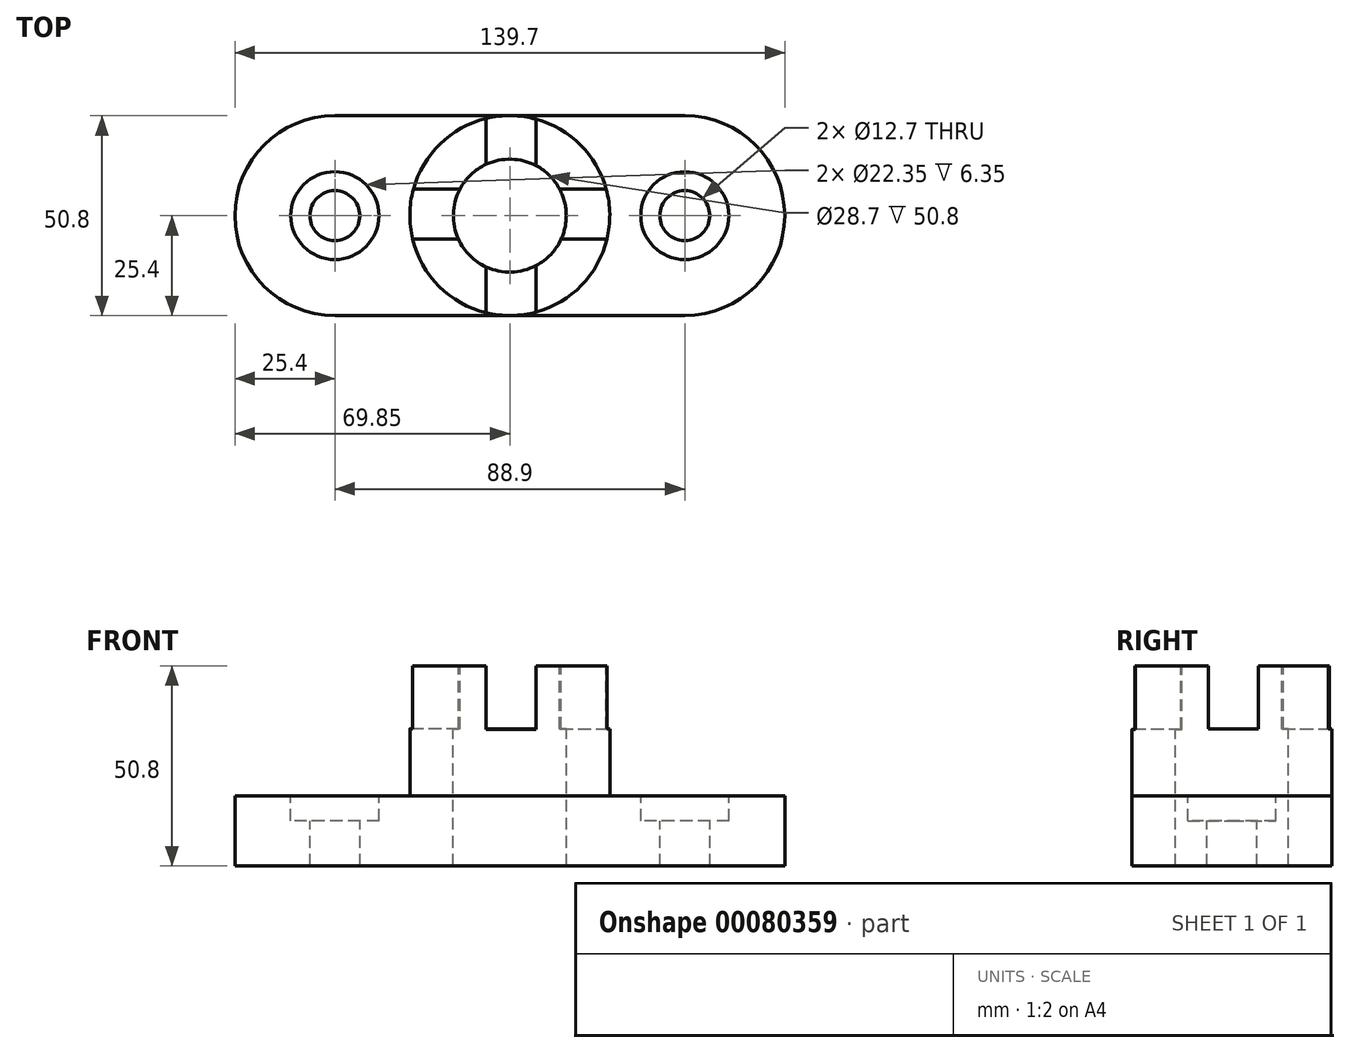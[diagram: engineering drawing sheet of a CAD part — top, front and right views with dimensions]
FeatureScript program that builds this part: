
annotation { "Feature Type Name" : "Feature", "Feature Type Description" : "" }
export const myFeature = defineFeature(function(context is Context, id is Id, definition is map)
    precondition{}
    {
        {
            var Q0;
            Q0=qCreatedBy(makeId("Top.planeOp"),FACE);
            var sketch = newSketch(context, id + "F0", { "sketchPlane" : qUnion([Q0])});
            skLineSegment(sketch, "E0", {"start": v(0, 50.8) * mm, "end": v(88.9, 50.8) * mm});
            skLineSegment(sketch, "E1", {"start": v(0, 0) * mm, "end": v(88.9, 0) * mm});
            skArc(sketch, "E2", {"start": v(88.9, 50.8) * mm, "mid": v(114.3, 25.4) * mm, "end": v(88.9, 0) * mm});
            skArc(sketch, "E3", {"start": v(0, 50.8) * mm, "mid": v(-25.4, 25.4) * mm, "end": v(0, 0) * mm});
            skCircle(sketch, "E4", {"center": v(0, 25.4) * mm, "radius": 6.35 * mm});
            skCircle(sketch, "E5", {"center": v(88.9, 25.4) * mm, "radius": 6.35 * mm});
            skCircle(sketch, "E6", {"center": v(44.45, 25.4) * mm, "radius": 25.4 * mm});
            skPoint(sketch, "E6.centerSnap0", {"position": v(44.45, 0) * mm});
            skCircle(sketch, "E7", {"center": v(44.45, 25.4) * mm, "radius": 14.35 * mm});
            skSolve(sketch);
        }
        {
            var Q0;
            Q0=makeQuery(id+"F0.imprint","IMPRINT",FACE,{"disambiguationData":[TD([[makeQuery(id+"F0.imprint","IMPRINT",EDGE,{"derivedFrom":sQuery(id+"F0.wireOp",EDGE,"E0")}),-1.0]])]});
            var Q1;
            Q1=makeQuery(id+"F0.imprint","IMPRINT",FACE,{"disambiguationData":[TD([[makeQuery(id+"F0.imprint","IMPRINT",EDGE,{"derivedFrom":sQuery(id+"F0.wireOp",EDGE,"E6")}),1.0]])]});
            extrude(context, id + "F1", {"entities" : qUnion([Q0, Q1]), "oppositeDirection" : true, "depth" : 17.78 * mm});
        }
        {
            var Q0;
            Q0=makeQuery(id+"F0.imprint","IMPRINT",FACE,{"disambiguationData":[TD([[makeQuery(id+"F0.imprint","IMPRINT",EDGE,{"derivedFrom":sQuery(id+"F0.wireOp",EDGE,"E6")}),1.0]])]});
            extrude(context, id + "F2", {"entities" : qUnion([Q0]), "operationType" : NewBodyOperationType.ADD, "depth" : 33.02 * mm});
        }
        {
            var Q0;
            Q0=makeQuery(id+"F2.opExtrude","CAP_FACE",FACE,{"disambiguationData":[OSD([sQuery(id+"F0.wireOp",EDGE,"E6"),sQuery(id+"F0.wireOp",EDGE,"E7")])],"isStart":false});
            var sketch = newSketch(context, id + "F3", { "sketchPlane" : qUnion([Q0])});
            skLineSegment(sketch, "E8", {"start": v(38.46, 12.36) * mm, "end": v(38.46, 0.72) * mm});
            skLineSegment(sketch, "E9", {"start": v(51.16, 12.71) * mm, "end": v(51.16, 0.9) * mm});
            skLineSegment(sketch, "E10", {"start": v(38.46, 38.44) * mm, "end": v(38.46, 50.08) * mm});
            skLineSegment(sketch, "E11", {"start": v(51.16, 38.09) * mm, "end": v(51.16, 49.9) * mm});
            skLineSegment(sketch, "E12", {"start": v(31.4, 19.4) * mm, "end": v(19.77, 19.4) * mm});
            skLineSegment(sketch, "E13", {"start": v(57.5, 19.4) * mm, "end": v(69.13, 19.4) * mm});
            skLineSegment(sketch, "E14", {"start": v(31.76, 32.1) * mm, "end": v(19.95, 32.1) * mm});
            skLineSegment(sketch, "E15", {"start": v(57.14, 32.1) * mm, "end": v(68.95, 32.1) * mm});
            skSolve(sketch);
        }
        {
            var Q0;
            {var subQ0=sQuery(id+"F3.wireOp",EDGE,"E13");Q0=makeQuery(id+"F3.imprint","IMPRINT",FACE,{"disambiguationData":[TD([[makeQuery(id+"F3.imprint","IMPRINT",EDGE,{"derivedFrom":subQ0}),1.0]])]});}
            extrude(context, id + "F4", {"entities" : qUnion([Q0]), "operationType" : NewBodyOperationType.REMOVE, "oppositeDirection" : true, "depth" : 16 * mm});
        }
        {
            var Q0;
            {var subQ0=sQuery(id+"F3.wireOp",EDGE,"E8");Q0=makeQuery(id+"F3.imprint","IMPRINT",FACE,{"disambiguationData":[TD([[makeQuery(id+"F3.imprint","IMPRINT",EDGE,{"derivedFrom":subQ0}),1.0]])]});}
            extrude(context, id + "F5", {"entities" : qUnion([Q0]), "operationType" : NewBodyOperationType.REMOVE, "oppositeDirection" : true, "depth" : 16.08 * mm});
        }
        {
            var Q0;
            {var subQ0=sQuery(id+"F3.wireOp",EDGE,"E12");Q0=makeQuery(id+"F3.imprint","IMPRINT",FACE,{"disambiguationData":[TD([[makeQuery(id+"F3.imprint","IMPRINT",EDGE,{"derivedFrom":subQ0}),-1.0]])]});}
            extrude(context, id + "F6", {"entities" : qUnion([Q0]), "operationType" : NewBodyOperationType.REMOVE, "oppositeDirection" : true, "depth" : 16 * mm});
        }
        {
            var Q0;
            {var subQ0=sQuery(id+"F3.wireOp",EDGE,"E10");Q0=makeQuery(id+"F3.imprint","IMPRINT",FACE,{"disambiguationData":[TD([[makeQuery(id+"F3.imprint","IMPRINT",EDGE,{"derivedFrom":subQ0}),-1.0]])]});}
            extrude(context, id + "F7", {"entities" : qUnion([Q0]), "operationType" : NewBodyOperationType.REMOVE, "oppositeDirection" : true, "depth" : 16 * mm});
        }
        {
            var Q0;
            Q0=qCreatedBy(makeId("Top.planeOp"),FACE);
            var sketch = newSketch(context, id + "F8", { "sketchPlane" : qUnion([Q0])});
            skCircle(sketch, "E16", {"center": v(0, 25.4) * mm, "radius": 6.35 * mm});
            skCircle(sketch, "E17", {"center": v(88.9, 25.4) * mm, "radius": 6.35 * mm});
            skCircle(sketch, "E18", {"center": v(0, 25.4) * mm, "radius": 11.18 * mm});
            skCircle(sketch, "E19", {"center": v(88.9, 25.4) * mm, "radius": 11.18 * mm});
            skSolve(sketch);
        }
        {
            var Q0;
            Q0=makeQuery(id+"F8.imprint","IMPRINT",FACE,{"disambiguationData":[TD([[makeQuery(id+"F8.imprint","IMPRINT",EDGE,{"derivedFrom":sQuery(id+"F8.wireOp",EDGE,"E16")}),-1.0]])]});
            var Q1;
            Q1=makeQuery(id+"F8.imprint","IMPRINT",FACE,{"disambiguationData":[TD([[makeQuery(id+"F8.imprint","IMPRINT",EDGE,{"derivedFrom":sQuery(id+"F8.wireOp",EDGE,"E17")}),-1.0]])]});
            extrude(context, id + "F9", {"entities" : qUnion([Q0, Q1]), "operationType" : NewBodyOperationType.REMOVE, "oppositeDirection" : true, "depth" : 6.35 * mm});
        }
    });
